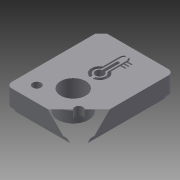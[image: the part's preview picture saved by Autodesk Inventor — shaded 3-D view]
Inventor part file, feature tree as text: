
AUTODESK INVENTOR PART (.ipt)
format: ipt  version: 2015 SP1 (Build 190203100, 203)  size: 236,544 bytes
history: native  units: mm
features: sketch x7, extrude x5, reference x4, other x2
ambient origin geometry x8: Origin, YZ Plane, XZ Plane, XY Plane, X Axis, Y Axis, Z Axis, Center Point
bodies: Body1 (feature_tree)
feature tree (18):
  other  "Sólido1"
  sketch  "Boceto1"  dims[d0=3.0mm d1=0.0mm]
  extrude  "Extrusión1"  Depth=1.0mm
  sketch  "Boceto3"  dims[d9=9.0mm d10=3.0mm d11=0.0mm]
  other  "Labio1"
  extrude  "Extrusión2"  Depth=3.0mm TaperAngle=0.0deg
  sketch  "Boceto7"
  extrude  "Extrusión3"  Depth=4.0mm TaperAngle=0.0deg
  extrude  "Extrusión4"  Depth=0.618mm
  extrude  "Extrusión5"  Depth=10.0mm TaperAngle=0.0deg
  sketch  "Boceto2"  dims[d2=1.0mm d3=1.0mm d4=0.0mm d5=0.0mm d6=0.0mm d7=0.0mm d8=9.5mm]
  reference  "Referencia1"
  reference  "Referencia2"
  sketch  "Boceto4"  dims[d12=11.0mm d13=4.0mm d14=0.0mm]
  reference  "Referencia3"
  reference  "Referencia4"
  sketch  "Boceto5"  dims[d16=10.0mm d17=0.0mm d31=0.618mm]
  sketch  "Boceto6"  dims[d35=1.0mm d36=10.0mm d37=0.0mm]
